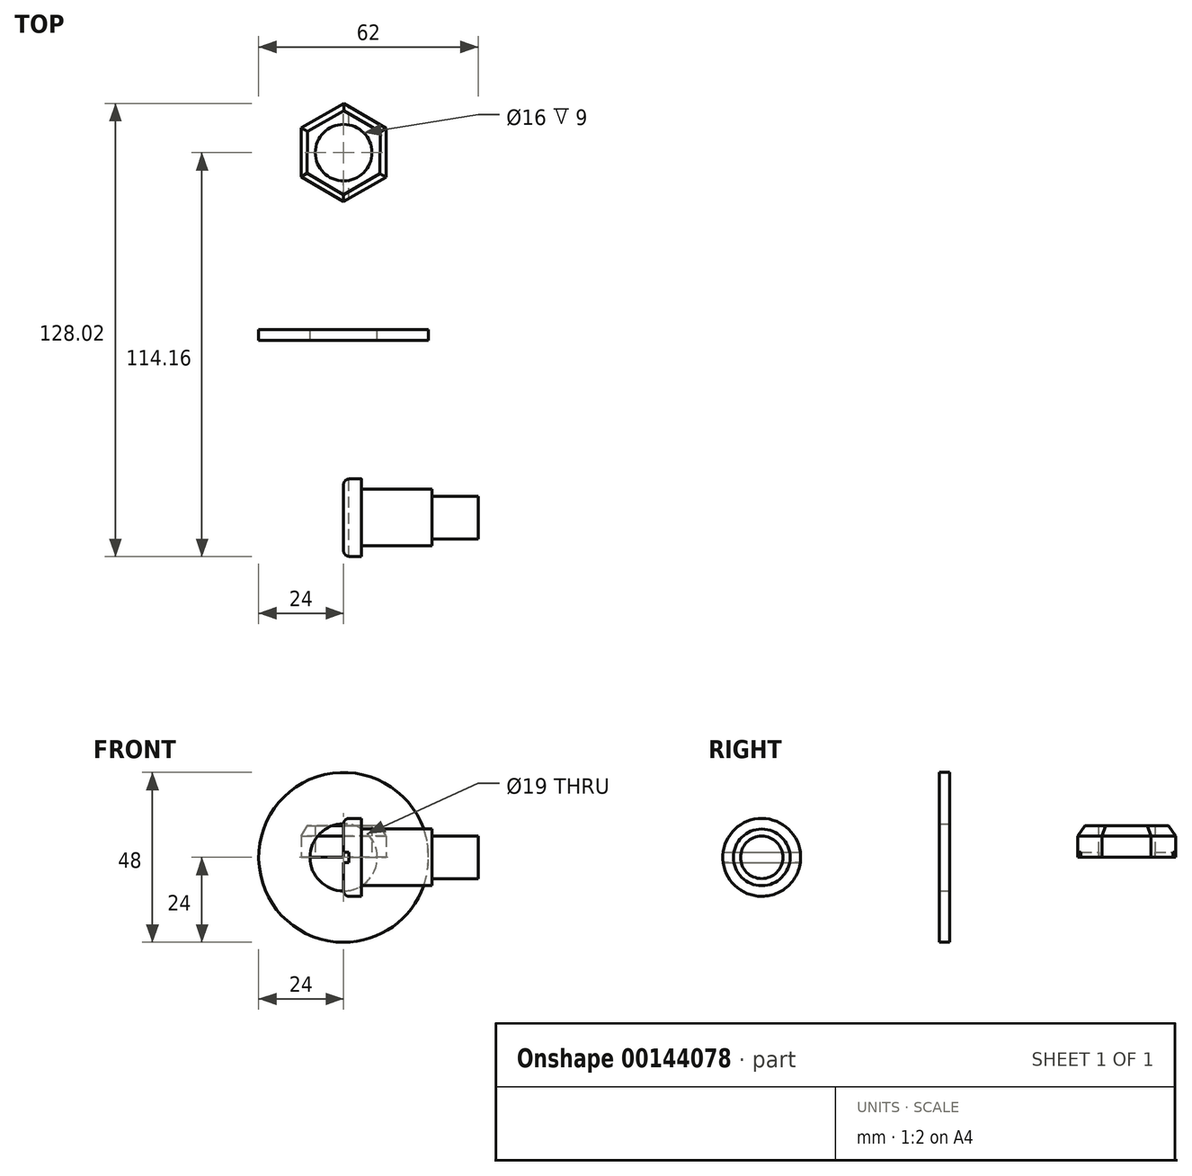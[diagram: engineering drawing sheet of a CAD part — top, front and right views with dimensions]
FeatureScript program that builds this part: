
annotation { "Feature Type Name" : "Feature", "Feature Type Description" : "" }
export const myFeature = defineFeature(function(context is Context, id is Id, definition is map)
    precondition{}
    {
        {
            var Q0;
            Q0=qCreatedBy(makeId("Front.planeOp"),FACE);
            var sketch = newSketch(context, id + "F0", { "sketchPlane" : qUnion([Q0])});
            skCircle(sketch, "E0", {"center": v(0, 0) * mm, "radius": 24 * mm});
            skCircle(sketch, "E1", {"center": v(0, 0) * mm, "radius": 9.5 * mm});
            skSolve(sketch);
        }
        {
            var Q0;
            Q0 = qSketchRegion(id + "F0", true);
            extrude(context, id + "F1", {"entities" : qUnion([Q0]), "depth" : 3 * mm});
        }
        {
            var Q0;
            Q0=qCreatedBy(makeId("Top.planeOp"),FACE);
            var sketch = newSketch(context, id + "F2", { "sketchPlane" : qUnion([Q0])});
            skLineSegment(sketch, "E2", {"start": v(0, 0) * mm, "end": v(0, 50) * mm, "construction": true});
            skCircle(sketch, "E3.cCircle", {"center": v(0, 50) * mm, "radius": 12 * mm, "construction": true});
            skLineSegment(sketch, "E3.0", {"start": v(-11.96, 57) * mm, "end": v(0.07, 63.86) * mm});
            skLineSegment(sketch, "E3.1", {"start": v(0.07, 63.86) * mm, "end": v(12.04, 56.86) * mm});
            skLineSegment(sketch, "E3.2", {"start": v(12.04, 56.86) * mm, "end": v(11.96, 43) * mm});
            skLineSegment(sketch, "E3.3", {"start": v(11.96, 43) * mm, "end": v(-0.07, 36.14) * mm});
            skLineSegment(sketch, "E3.4", {"start": v(-0.07, 36.14) * mm, "end": v(-12.04, 43.14) * mm});
            skLineSegment(sketch, "E3.5", {"start": v(-12.04, 43.14) * mm, "end": v(-11.96, 57) * mm});
            skPoint(sketch, "E3.0.midPoint", {"position": v(-5.94, 60.42) * mm});
            skCircle(sketch, "E4", {"center": v(0, 50) * mm, "radius": 8 * mm});
            skSolve(sketch);
        }
        {
            var Q0;
            Q0 = qSketchRegion(id + "F2", true);
            extrude(context, id + "F3", {"entities" : qUnion([Q0]), "depth" : 9 * mm});
        }
        {
            var Q0;
            Q0=makeQuery(id+"F3.opExtrude","CAP_EDGE",EDGE,{"disambiguationData":[OSD([sQuery(id+"F2.wireOp",EDGE,"E3.2")])],"isStart":false});
            var Q1;
            Q1=makeQuery(id+"F3.opExtrude","CAP_EDGE",EDGE,{"disambiguationData":[OSD([sQuery(id+"F2.wireOp",EDGE,"E3.3")])],"isStart":false});
            var Q2;
            Q2=makeQuery(id+"F3.opExtrude","CAP_EDGE",EDGE,{"disambiguationData":[OSD([sQuery(id+"F2.wireOp",EDGE,"E3.4")])],"isStart":false});
            var Q3;
            Q3=makeQuery(id+"F3.opExtrude","CAP_EDGE",EDGE,{"disambiguationData":[OSD([sQuery(id+"F2.wireOp",EDGE,"E3.1")])],"isStart":false});
            var Q4;
            Q4=makeQuery(id+"F3.opExtrude","CAP_EDGE",EDGE,{"disambiguationData":[OSD([sQuery(id+"F2.wireOp",EDGE,"E3.0")])],"isStart":false});
            var Q5;
            Q5=makeQuery(id+"F3.opExtrude","CAP_EDGE",EDGE,{"disambiguationData":[OSD([sQuery(id+"F2.wireOp",EDGE,"E3.5")])],"isStart":false});
            chamfer(context, id + "F4", {"entities" : qUnion([Q0, Q1, Q2, Q3, Q4, Q5]), "chamferType" : ChamferType.OFFSET_ANGLE, "width" : 3 * mm, "oppositeDirection" : false, "angle" : 30 * degree, "tangentPropagation" : true});
        }
        {
            var Q0;
            Q0=qCreatedBy(makeId("Right.planeOp"),FACE);
            var sketch = newSketch(context, id + "F5", { "sketchPlane" : qUnion([Q0])});
            skLineSegment(sketch, "E5", {"start": v(0, 0) * mm, "end": v(-53.16, 0) * mm, "construction": true});
            skCircle(sketch, "E6", {"center": v(-53.16, 0) * mm, "radius": 11 * mm});
            skSolve(sketch);
        }
        {
            var Q0;
            Q0 = qSketchRegion(id + "F5", true);
            extrude(context, id + "F6", {"entities" : qUnion([Q0]), "depth" : 5 * mm});
        }
        {
            var Q0;
            Q0=makeQuery(id+"F6.opExtrude","CAP_FACE",FACE,{"disambiguationData":[OSD([sQuery(id+"F5.wireOp",EDGE,"E6")])],"isStart":false});
            var sketch = newSketch(context, id + "F7", { "sketchPlane" : qUnion([Q0])});
            skCircle(sketch, "E7", {"center": v(-53.16, 0) * mm, "radius": 8 * mm});
            skSolve(sketch);
        }
        {
            var Q0;
            Q0 = qSketchRegion(id + "F7", true);
            extrude(context, id + "F8", {"entities" : qUnion([Q0]), "operationType" : NewBodyOperationType.ADD, "depth" : 20 * mm});
        }
        {
            var Q0;
            Q0=makeQuery(id+"F8.opExtrude","CAP_FACE",FACE,{"disambiguationData":[OSD([sQuery(id+"F7.wireOp",EDGE,"E7")])],"isStart":false});
            var sketch = newSketch(context, id + "F9", { "sketchPlane" : qUnion([Q0])});
            skCircle(sketch, "E8", {"center": v(-53.16, 0) * mm, "radius": 6 * mm});
            skSolve(sketch);
        }
        {
            var Q0;
            Q0 = qSketchRegion(id + "F9", true);
            extrude(context, id + "F10", {"entities" : qUnion([Q0]), "operationType" : NewBodyOperationType.ADD, "depth" : 13 * mm});
        }
        {
            var Q0;
            Q0=sQuery(id+"F5.wireOp",VERTEX,"E5.end");
            var Q1;
            Q1=qCreatedBy(makeId("Front.planeOp"),FACE);
            cPlane(context, id + "F11", {"entities" : qUnion([Q0, Q1]), "cplaneType" : CPlaneType.PLANE_POINT, "offset" : 25 * mm, "width" : 150 * mm, "height" : 150 * mm});
        }
        {
            var Q0;
            Q0=qCreatedBy(id+"F11.planeOp",FACE);
            var sketch = newSketch(context, id + "F12", { "sketchPlane" : qUnion([Q0])});
            skLineSegment(sketch, "E9", {"start": v(0, 1.5) * mm, "end": v(1.5, 1.5) * mm});
            skLineSegment(sketch, "E10", {"start": v(1.5, 1.5) * mm, "end": v(1.5, -1.5) * mm});
            skLineSegment(sketch, "E11", {"start": v(1.5, -1.5) * mm, "end": v(0, -1.5) * mm});
            skLineSegment(sketch, "E12", {"start": v(0, -1.5) * mm, "end": v(0, 0) * mm});
            skLineSegment(sketch, "E13", {"start": v(0, 1.5) * mm, "end": v(0, -1.5) * mm});
            skSolve(sketch);
        }
        {
            var Q0;
            Q0 = qSketchRegion(id + "F12", true);
            extrude(context, id + "F13", {"entities" : qUnion([Q0]), "operationType" : NewBodyOperationType.REMOVE, "endBound" : BoundingType.THROUGH_ALL, "depth" : 25 * mm, "hasSecondDirection" : true, "secondDirectionBound" : SecondDirectionBoundingType.THROUGH_ALL, "secondDirectionOppositeDirection" : true, "secondDirectionDepth" : 25 * mm});
        }
        {
            var Q0;
            {var subQ0=sQuery(id+"F5.wireOp",EDGE,"E6");Q0=makeQuery(id+"F13.boolean.opBoolean","SPLIT",EDGE,{"disambiguationData":[TD([makeQuery(id+"F13.opExtrude","SWEPT_FACE",FACE,{"disambiguationData":[OSD([sQuery(id+"F12.wireOp",EDGE,"E9")])]})])],"derivedFrom":makeQuery(id+"F6.opExtrude","CAP_EDGE",EDGE,{"disambiguationData":[OSD([subQ0])],"isStart":true})});}
            var Q1;
            {var subQ0=sQuery(id+"F5.wireOp",EDGE,"E6");Q1=makeQuery(id+"F13.boolean.opBoolean","SPLIT",EDGE,{"disambiguationData":[TD([makeQuery(id+"F13.opExtrude","SWEPT_FACE",FACE,{"disambiguationData":[OSD([sQuery(id+"F12.wireOp",EDGE,"E11")])]})])],"derivedFrom":makeQuery(id+"F6.opExtrude","CAP_EDGE",EDGE,{"disambiguationData":[OSD([subQ0])],"isStart":true})});}
            fillet(context, id + "F14", {"entities" : qUnion([Q0, Q1]), "radius" : 1.5 * mm, "tangentPropagation" : true, "allowEdgeOverflow" : false});
        }
    });
